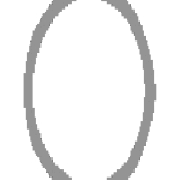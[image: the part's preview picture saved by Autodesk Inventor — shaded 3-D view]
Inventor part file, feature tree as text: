
AUTODESK INVENTOR PART (.ipt)
format: ipt  version: 2021 (Build 250183000, 183)  size: 112,640 bytes
history: native  units: in
note: dims shown in document units (in); Inventor stores cm internally (conversion verified against a paired STEP export)
features: other x4, sketch x3, plane x1
ambient origin geometry x8: Origin, YZ Plane, XZ Plane, XY Plane, X Axis, Y Axis, Z Axis, Center Point
bodies: Solid1 (feature_tree), Body (feature_tree)
feature tree (8):
  other  "Driven Length"
  other  "Frame Generator"
  other  "Start Plane"
  other  "End Plane"
  sketch  "Sketch"  dims[d2=16.0in d4=-0.0in d5=16.0in d6=0.12in d7=0.0in d8=90.0deg d9=16.0in]
  sketch  "Sketch2"  dims[d0=1.0in]
  plane  "Work Plane3"
  sketch  "Sketch3"  dims[d1=0.065in]
